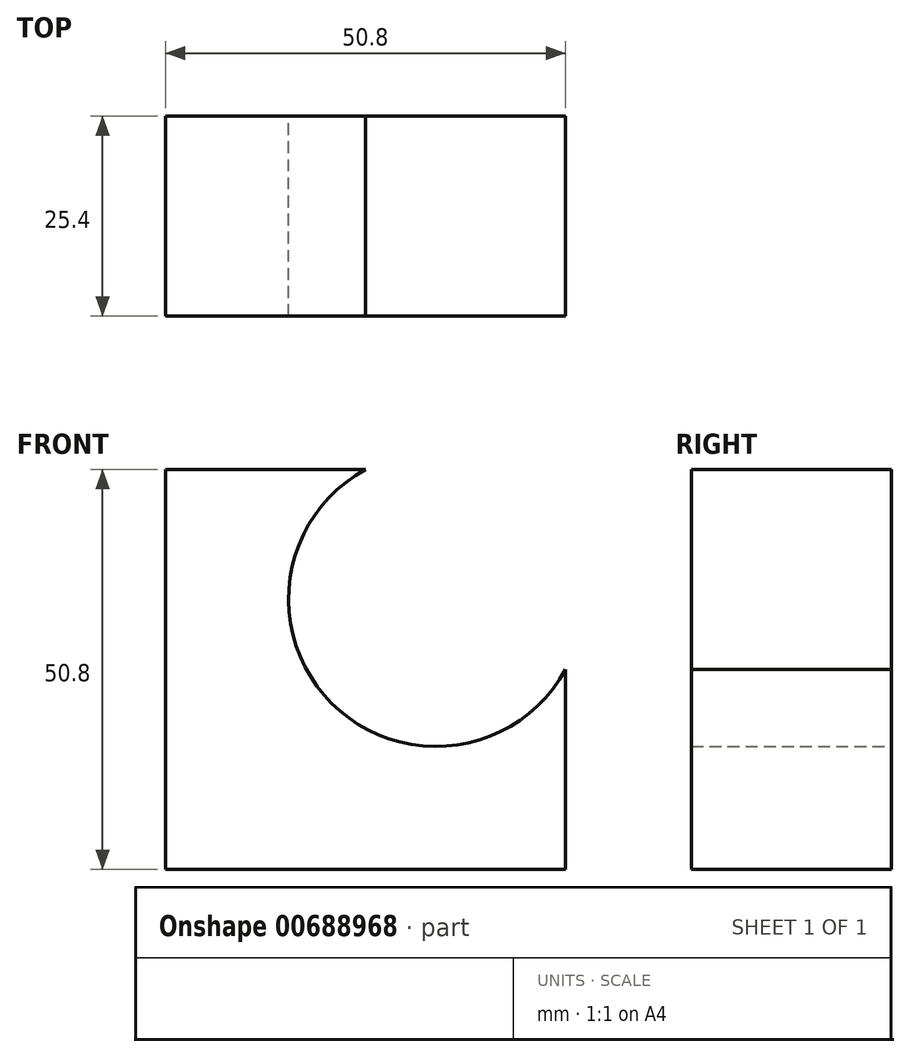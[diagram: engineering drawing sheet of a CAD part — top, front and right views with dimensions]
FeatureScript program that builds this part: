
annotation { "Feature Type Name" : "Feature", "Feature Type Description" : "" }
export const myFeature = defineFeature(function(context is Context, id is Id, definition is map)
    precondition{}
    {
        {
            var Q0;
            Q0=qCreatedBy(makeId("Front.planeOp"),FACE);
            var sketch = newSketch(context, id + "F0", { "sketchPlane" : qUnion([Q0])});
            skLineSegment(sketch, "E0", {"start": v(0, 83.17) * mm, "end": v(-25.4, 83.17) * mm});
            skLineSegment(sketch, "E1", {"start": v(-25.4, 83.17) * mm, "end": v(-25.4, 32.37) * mm});
            skLineSegment(sketch, "E2", {"start": v(-25.4, 32.37) * mm, "end": v(25.4, 32.37) * mm});
            skLineSegment(sketch, "E3", {"start": v(25.4, 32.37) * mm, "end": v(25.4, 57.77) * mm});
            skArc(sketch, "E4", {"start": v(0, 83.17) * mm, "mid": v(-4.3, 53.48) * mm, "end": v(25.4, 57.77) * mm});
            skSolve(sketch);
        }
        {
            var Q0;
            Q0 = qSketchRegion(id + "F0", true);
            extrude(context, id + "F1", {"entities" : qUnion([Q0]), "depth" : 25.4 * mm, "offsetDistance" : 25.4 * mm});
        }
    });
